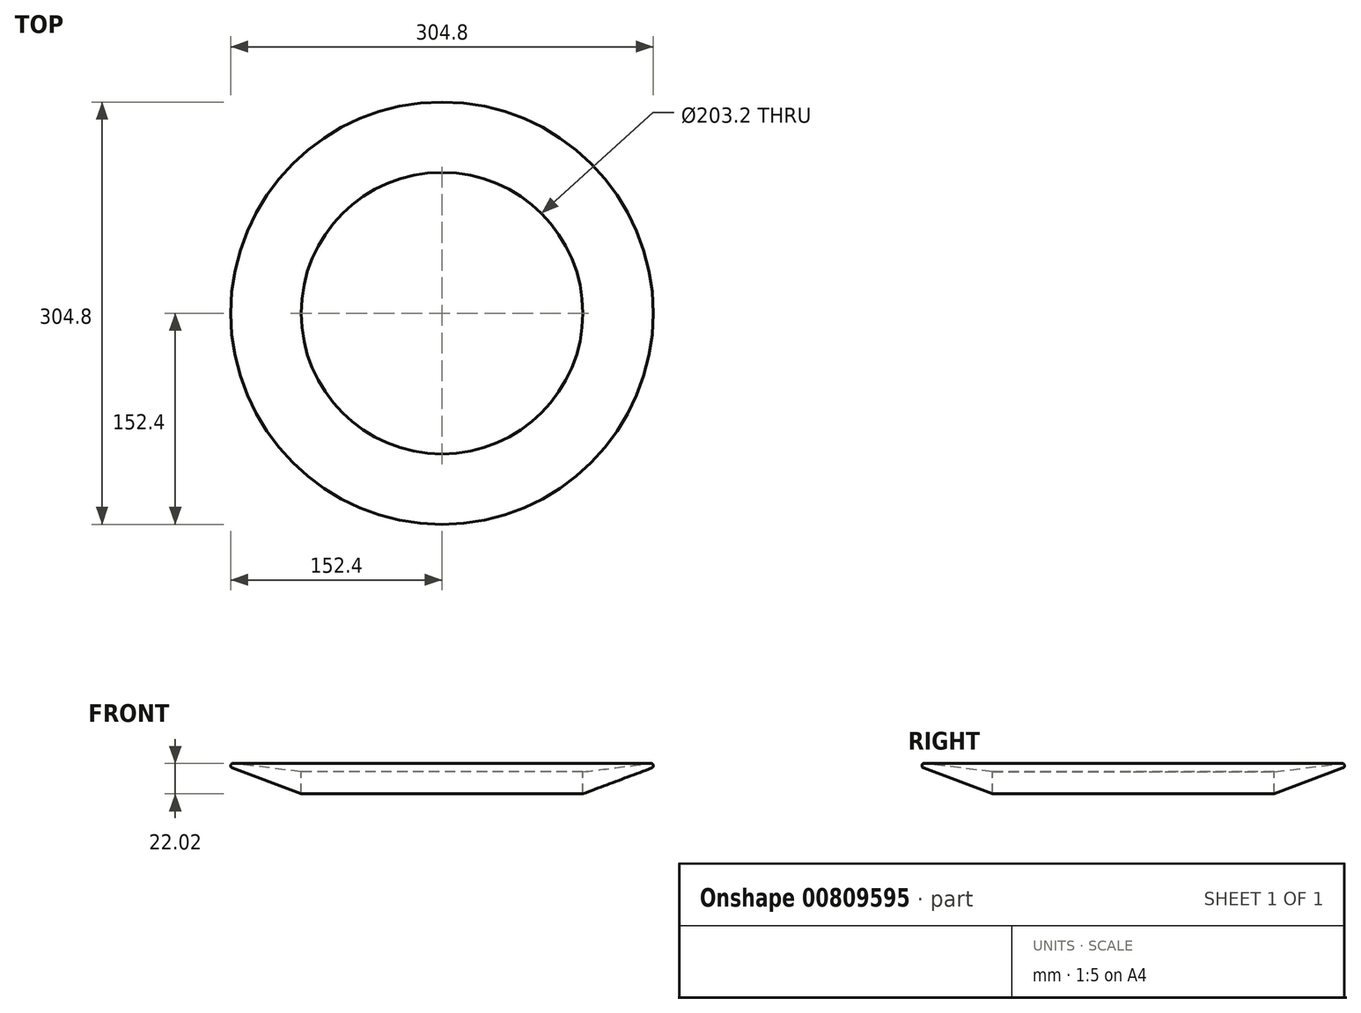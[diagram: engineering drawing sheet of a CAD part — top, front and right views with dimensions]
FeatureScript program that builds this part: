
annotation { "Feature Type Name" : "Feature", "Feature Type Description" : "" }
export const myFeature = defineFeature(function(context is Context, id is Id, definition is map)
    precondition{}
    {
        {
            var Q0;
            Q0=qCreatedBy(makeId("Front.planeOp"),FACE);
            var sketch = newSketch(context, id + "F0", { "sketchPlane" : qUnion([Q0])});
            skPoint(sketch, "E0.orphan", {"position": v(0, 0) * mm});
            skPoint(sketch, "E1.orphan", {"position": v(152.4, 0) * mm});
            skPoint(sketch, "E2.start.orphan", {"position": v(76.2, 0) * mm});
            skLineSegment(sketch, "E3", {"start": v(0, 0) * mm, "end": v(0, -25.4) * mm});
            skLineSegment(sketch, "E4", {"start": v(101.6, 0) * mm, "end": v(152.4, 6.35) * mm});
            skLineSegment(sketch, "E5", {"start": v(152.4, 6.35) * mm, "end": v(152.4, 3.17) * mm});
            skLineSegment(sketch, "E6", {"start": v(101.6, -15.87) * mm, "end": v(152.4, 3.17) * mm});
            skLineSegment(sketch, "E7", {"start": v(101.6, 0) * mm, "end": v(101.6, -15.87) * mm});
            skSolve(sketch);
        }
        {
            var Q0;
            Q0=makeQuery(id+"F0.imprint","IMPRINT",FACE,{"disambiguationData":[TD([[makeQuery(id+"F0.imprint","IMPRINT",EDGE,{"derivedFrom":sQuery(id+"F0.wireOp",EDGE,"E4")}),-1.0]])]});
            var Q1;
            Q1=sQuery(id+"F0.wireOp",EDGE,"E3");
            revolve(context, id + "F1", {"surfaceOperationType" : NewSurfaceOperationType.NEW, "entities" : qUnion([Q0]), "axis" : qUnion([Q1]), "revolveType" : RevolveType.FULL});
        }
        {
            var Q0;
            Q0=makeQuery(id+"F1.opRevolve","SWEPT_EDGE",EDGE,{"disambiguationData":[OSD([sQuery(id+"F0.wireOp",EDGE,"E4"),sQuery(id+"F0.wireOp",EDGE,"E5")])]});
            var Q1;
            Q1=makeQuery(id+"F1.opRevolve","SWEPT_EDGE",EDGE,{"disambiguationData":[OSD([sQuery(id+"F0.wireOp",EDGE,"E5"),sQuery(id+"F0.wireOp",EDGE,"E6")])]});
            fillet(context, id + "F2", {"entities" : qUnion([Q0, Q1]), "radius" : 1.59 * mm, "tangentPropagation" : true, "allowEdgeOverflow" : false});
        }
    });
